# Revit family: Landscape-Forms_Motive_Area-Light
name_source: partatom
category: Lighting Fixtures
units: mm (PartAtom-declared; Revit-internal decimal feet)

## family parameters
Always vertical = Yes
Cut with Voids When Loaded = No
Light Source = Yes
OmniClass Number = 23.80.70.14.21
OmniClass Title = Street and Roadway Lighting
Part Type = Normal
Room Calculation Point = No
Round Connector Dimension = Use Diameter
Shared = No
Work Plane-Based = No

## types (2) — shared parameters
Apparent Load = 0 VA
Assembly Code = D5020280
Color Filter = 16777215
Default Elevation = 0' - 0"
Diffuser Lens = LANDSCAPE FORMS - DIFFUSER - ILLUMINATED - LED
Dimming Lamp Color Temperature Shift = <None>
Emit Shape Visible in Rendering = No
Emit from Circle Diameter = 1' - 0"
Lamp = LED Cartridge
Load Classification = Lighting - Exterior
Manufacturer = Landscape Forms
Model = AJ500-10
Number of Poles = 1
Photometric Web File = LF_Motive_Area_AJ500-LB-80F.ies
Tilt Angle = 90.00°
URL = https://www.landscapeforms.com
Voltage = 120 V
Wattage Comments = 31.7

## per-type parameters (varying)
| type | Description | Height |
| 10' | Motive Area Light, 10 ft. | 10' - 0" |
| 12' | Motive Area Light, 12 ft. | 12' - 0" |
